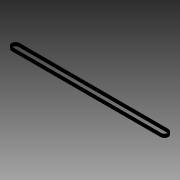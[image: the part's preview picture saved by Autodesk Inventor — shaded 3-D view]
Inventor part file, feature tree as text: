
AUTODESK INVENTOR PART (.ipt)
format: ipt  version: 2013 (Build 170138000, 138)  size: 88,576 bytes
history: native  units: mm
features: extrude x1, sketch x1
ambient origin geometry x8: Origin, YZ Plane, XZ Plane, XY Plane, X Axis, Y Axis, Z Axis, Center Point
bodies: Solid1 (feature_tree)
feature tree (2):
  extrude  "Extrusion1"  Depth=12.0mm
  sketch  "Sketch1"  dims[d0=12.0mm d2=12.0mm d3=279.0mm d4=1.2mm d5=6.0mm d6=0.0mm]
